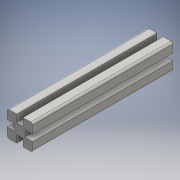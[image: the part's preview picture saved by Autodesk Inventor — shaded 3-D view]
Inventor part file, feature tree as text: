
AUTODESK INVENTOR PART (.ipt)
format: ipt  version: 2016 (Build 200138000, 138)  size: 120,320 bytes
history: native  units: mm
features: extrude x1, sketch x1
ambient origin geometry x8: Origin, YZ Plane, XZ Plane, XY Plane, X Axis, Y Axis, Z Axis, Center Point
bodies: Solid1 (feature_tree)
feature tree (2):
  extrude  "Extrusion1"  [1 undecoded]
  sketch  "Sketch1"  dims[d0=220.0mm d1=0.0mm]
note: 1 required parameter value undecoded (feature->parameter linkage not recoverable at this tier; creation-order binding heuristic only, values carry confidence <= 0.55)
